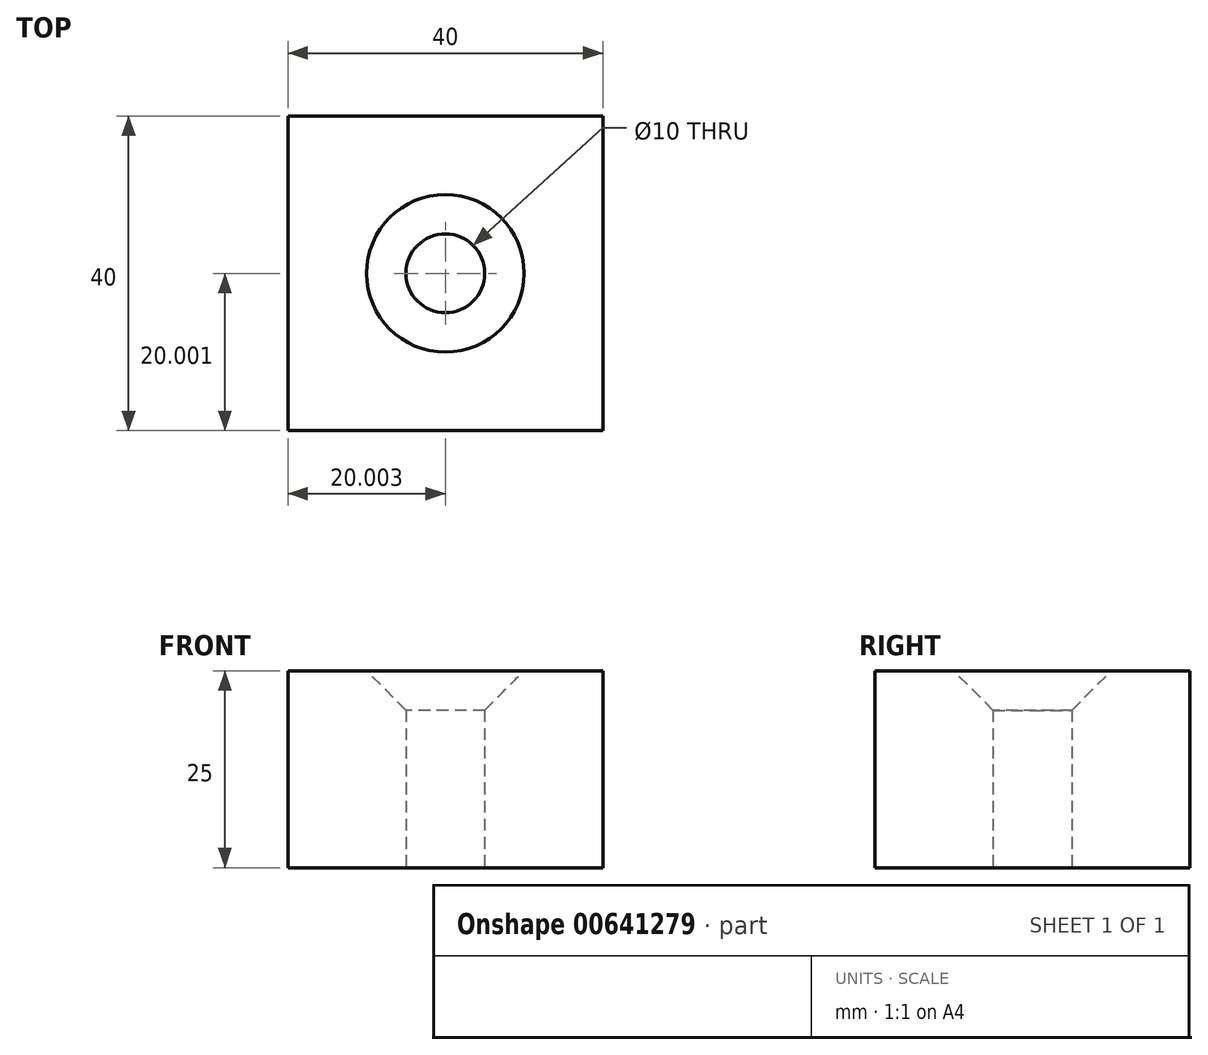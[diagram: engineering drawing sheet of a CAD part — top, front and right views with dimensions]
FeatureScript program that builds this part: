
annotation { "Feature Type Name" : "Feature", "Feature Type Description" : "" }
export const myFeature = defineFeature(function(context is Context, id is Id, definition is map)
    precondition{}
    {
        {
            var Q0;
            Q0=qCreatedBy(makeId("Top.planeOp"),FACE);
            var sketch = newSketch(context, id + "F0", { "sketchPlane" : qUnion([Q0])});
            skLineSegment(sketch, "E0.bottom", {"start": v(-23.7, 24.6) * mm, "end": v(16.3, 24.6) * mm});
            skLineSegment(sketch, "E0.top", {"start": v(-23.7, -15.4) * mm, "end": v(16.3, -15.4) * mm});
            skLineSegment(sketch, "E0.left", {"start": v(-23.7, 24.6) * mm, "end": v(-23.7, -15.4) * mm});
            skLineSegment(sketch, "E0.right", {"start": v(16.3, 24.6) * mm, "end": v(16.3, -15.4) * mm});
            skCircle(sketch, "E1", {"center": v(-3.7, 4.6) * mm, "radius": 5 * mm});
            skPoint(sketch, "E1.centerSnap0", {"position": v(-23.7, 4.6) * mm});
            skPoint(sketch, "E1.centerSnap1", {"position": v(-3.7, 24.6) * mm});
            skSolve(sketch);
        }
        {
            var Q0;
            Q0=makeQuery(id+"F0.imprint","IMPRINT",FACE,{"disambiguationData":[TD([[makeQuery(id+"F0.imprint","IMPRINT",EDGE,{"derivedFrom":sQuery(id+"F0.wireOp",EDGE,"E0.bottom")}),-1.0]])]});
            extrude(context, id + "F1", {"entities" : qUnion([Q0]), "depth" : 25 * mm, "offsetDistance" : 25 * mm});
        }
        {
            var Q0;
            Q0=makeQuery(id+"F1.opExtrude","CAP_EDGE",EDGE,{"disambiguationData":[OSD([sQuery(id+"F0.wireOp",EDGE,"E1")])],"isStart":false});
            chamfer(context, id + "F2", {"entities" : qUnion([Q0]), "width" : 5 * mm, "tangentPropagation" : true});
        }
    });
